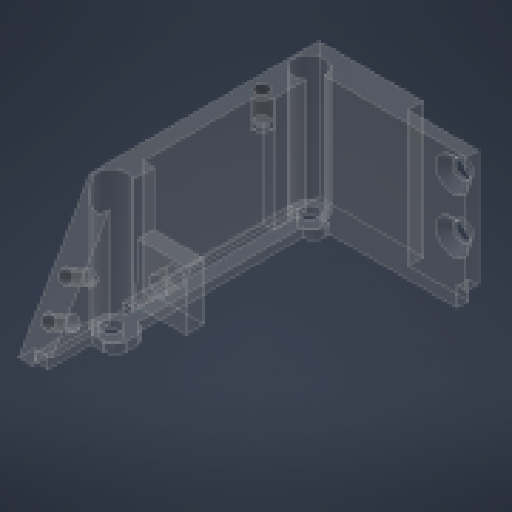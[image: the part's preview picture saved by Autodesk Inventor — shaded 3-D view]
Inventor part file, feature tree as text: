
AUTODESK INVENTOR PART (.ipt)
format: ipt  version: 2023 (Build 270158000, 158)  size: 358,912 bytes
history: native  units: mm
features: sketch x11, extrude x8, hole x5, other x1, fillet x1
ambient origin geometry x8: Origin, YZ Plane, XZ Plane, XY Plane, X Axis, Y Axis, Z Axis, Center Point
bodies: Body1 (feature_tree)
feature tree (26):
  other  "Bryła1"
  extrude  "Wyciągnięcie proste1"  Depth=58.0mm
  extrude  "Wyciągnięcie proste2"  Depth=5.0mm
  extrude  "Wyciągnięcie proste3"  Depth=5.0mm
  hole  "Otwór1"  [1 undecoded]
  hole  "Otwór2"  [1 undecoded]
  hole  "Otwór3"  [1 undecoded]
  extrude  "Wyciągnięcie proste4"  Depth=25.0mm TaperAngle=0.0deg
  fillet  "Zaokrąglenie1"  Radius=2.0mm
  sketch  "Szkic7"
  hole  "Otwór4"  [1 undecoded]
  extrude  "Wyciągnięcie proste5"  Depth=5.2mm
  extrude  "Wyciągnięcie proste7"  TaperAngle=60.0deg  [1 undecoded]
  sketch  "Szkic10"
  extrude  "Wyciągnięcie proste6"  Depth=25.0mm TaperAngle=0.0deg
  extrude  "Wyciągnięcie proste8"  Depth=4.5mm
  hole  "Otwór5"  [1 undecoded]
  sketch  "Szkic1"
  sketch  "Szkic2"
  sketch  "Szkic3"
  sketch  "Szkic4"
  sketch  "Szkic5"
  sketch  "Szkic6"
  sketch  "Szkic8"
  sketch  "Szkic9"
  sketch  "Szkic11"
note: 6 required parameter values undecoded (feature->parameter linkage not recoverable at this tier; creation-order binding heuristic only, values carry confidence <= 0.55)
